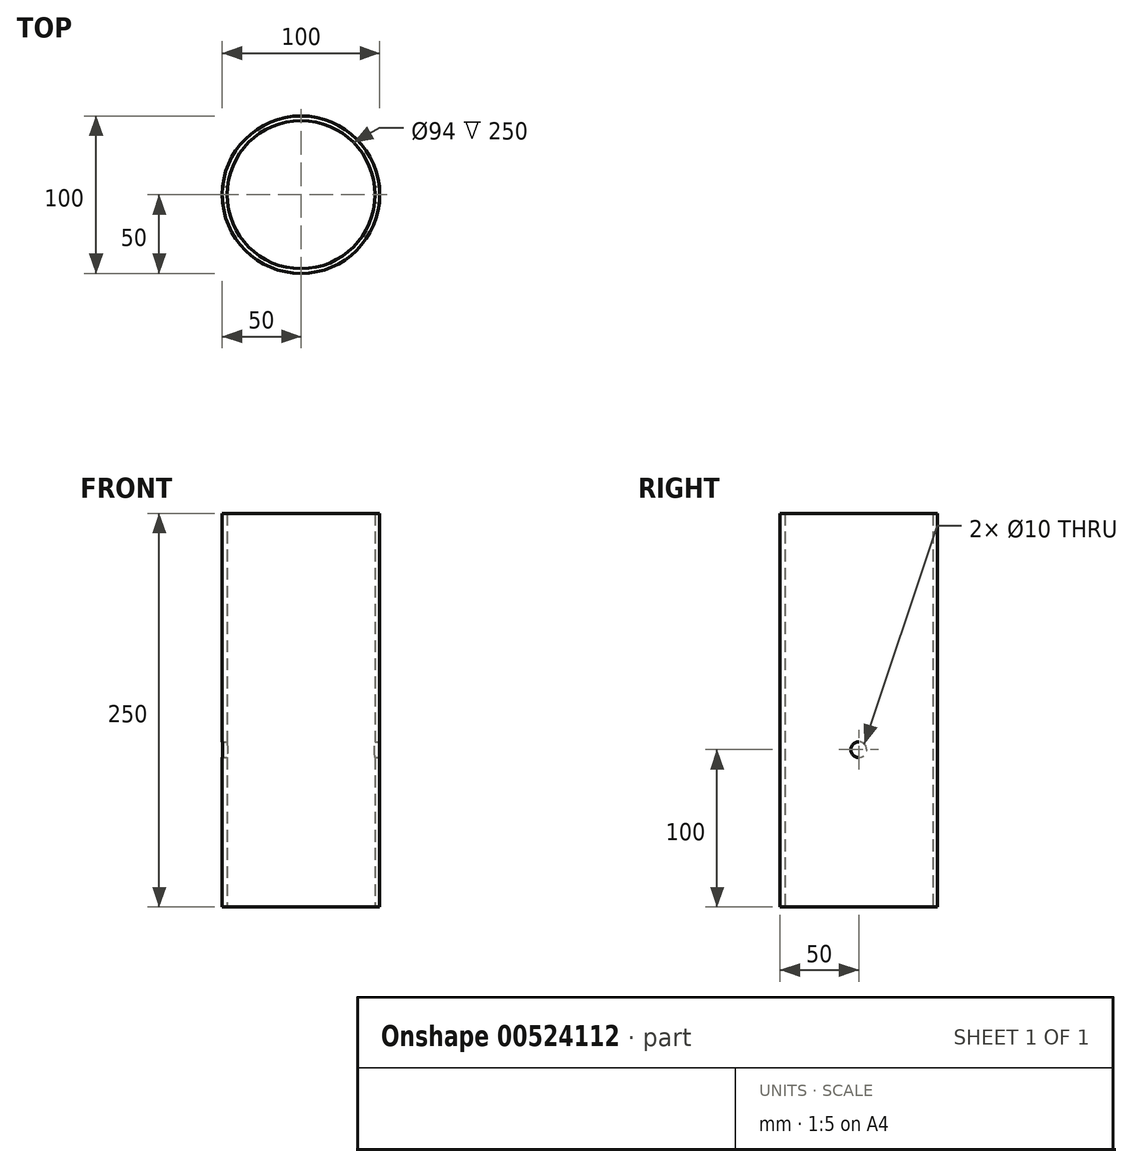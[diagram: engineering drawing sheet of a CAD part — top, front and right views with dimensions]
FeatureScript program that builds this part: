
annotation { "Feature Type Name" : "Feature", "Feature Type Description" : "" }
export const myFeature = defineFeature(function(context is Context, id is Id, definition is map)
    precondition{}
    {
        {
            var Q0;
            Q0=qCreatedBy(makeId("Top.planeOp"),FACE);
            var sketch = newSketch(context, id + "F0", { "sketchPlane" : qUnion([Q0])});
            skCircle(sketch, "E0", {"center": v(0, 0) * mm, "radius": 50 * mm});
            skCircle(sketch, "E1", {"center": v(0, 0) * mm, "radius": 47 * mm});
            skSolve(sketch);
        }
        {
            var Q0;
            Q0=qSketchRegion(id+"F0",true);
            extrude(context, id + "F1", {"entities" : qUnion([Q0]), "depth" : 250 * mm});
        }
        {
            var Q0;
            Q0=qCreatedBy(makeId("Right.planeOp"),FACE);
            var sketch = newSketch(context, id + "F2", { "sketchPlane" : qUnion([Q0])});
            skCircle(sketch, "E2", {"center": v(0, 100) * mm, "radius": 5 * mm});
            skSolve(sketch);
        }
        {
            var Q0;
            Q0=qSketchRegion(id+"F2",true);
            extrude(context, id + "F3", {"entities" : qUnion([Q0]), "operationType" : NewBodyOperationType.REMOVE, "oppositeDirection" : true, "depth" : 200 * mm, "symmetric" : true});
        }
    });
